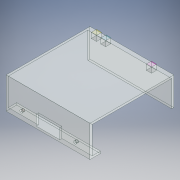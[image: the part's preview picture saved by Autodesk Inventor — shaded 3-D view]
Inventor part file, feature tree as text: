
AUTODESK INVENTOR PART (.ipt)
format: ipt  version: 2018 (Build 220112000, 112)  size: 182,784 bytes
history: native  units: in
note: dims shown in document units (in); Inventor stores cm internally (conversion verified against a paired STEP export)
features: extrude x4, sketch x4, fillet x1
ambient origin geometry x8: Origin, YZ Plane, XZ Plane, XY Plane, X Axis, Y Axis, Z Axis, Center Point
bodies: Solid1 (feature_tree)
feature tree (9):
  extrude  "Extrusion1"  Depth=2.126in
  extrude  "Extrusion2"  Depth=0.7874in
  extrude  "Extrusion3"  Depth=0.1575in
  fillet  "Fillet1"  Radius=0.1575in
  extrude  "Extrusion4"  Depth=0.1575in
  sketch  "Sketch1"  dims[d0=6.2992in d1=2.126in]
  sketch  "Sketch2"  dims[d2=2.3622in d3=0.7874in]
  sketch  "Sketch3"  dims[d4=0.1575in d5=0.1575in d6=0.1575in]
  sketch  "Sketch4"  dims[d7=0.1575in d8=0.1575in d9=0.1575in d10=6.2992in d11=0.0in d12=1.7717in d13=0.1575in d14=0.7874in d15=3.1496in d16=0.1969in d17=0.0in d18=0.1969in d19=2.2638in d20=1.1319in d21=1.1319in d22=0.7874in d23=0.5512in d24=0.1575in d25=0.5512in d26=0.2165in d27=0.1969in d28=0.0in d29=0.0787in d30=0.3937in d31=0.0in d32=0.3937in d33=0.3937in d34=0.3937in d35=0.3937in]
